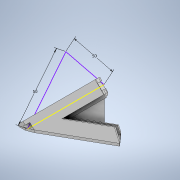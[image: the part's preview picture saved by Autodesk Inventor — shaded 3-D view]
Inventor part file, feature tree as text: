
AUTODESK INVENTOR PART (.ipt)
format: ipt  version: 2020 (Build 240168000, 168)  size: 267,776 bytes
history: native  units: mm
features: extrude x12, sketch x11, revolve x2, pattern_circular x1
ambient origin geometry x8: Origin, YZ Plane, XZ Plane, XY Plane, X Axis, Y Axis, Z Axis, Center Point
bodies: Solid1 (feature_tree)
feature tree (26):
  sketch  "Sketch1"  dims[d0=100.0mm d1=100.0mm]
  sketch  "Sketch2"  dims[d2=50.0mm d3=50.0mm]
  revolve  "Revolution1"  [1 undecoded]
  sketch  "Sketch3"  dims[d4=45.0deg d5=5.0mm d6=0.0mm]
  extrude  "Extrusion1"  Depth=50.0mm
  revolve  "Revolution2"  [1 undecoded]
  extrude  "Extrusion2"  Depth=5.0mm TaperAngle=0.0deg
  extrude  "Extrusion3"  Depth=5.0mm TaperAngle=90.0deg
  pattern_circular  "Circular Pattern1"  [2 undecoded]
  extrude  "Extrusion4"  Depth=5.0mm
  extrude  "Extrusion5"  Depth=2.0mm TaperAngle=0.0deg
  extrude  "Extrusion6"  Depth=27.0mm TaperAngle=0.0deg
  extrude  "Extrusion7"  Depth=2.0mm TaperAngle=0.0deg
  extrude  "Extrusion8"  [1 undecoded]
  extrude  "Extrusion9"  [1 undecoded]
  extrude  "Extrusion10"  [1 undecoded]
  extrude  "Extrusion11"  [1 undecoded]
  extrude  "Extrusion13"  [1 undecoded]
  sketch  "Sketch4"  dims[d7=45.0deg d8=5.0mm d9=0.0mm]
  sketch  "Sketch5"  dims[d10=5.0mm d11=0.0mm d12=20.0mm d13=90.0deg]
  sketch  "Sketch6"  dims[d15=7.0mm d16=0.0mm]
  sketch  "Sketch7"  dims[d17=44.0mm d18=0.0mm]
  sketch  "Sketch8"  dims[d19=3.0mm d20=0.0mm]
  sketch  "Sketch9"  dims[d21=2.0mm d22=0.0mm]
  sketch  "Sketch10"  dims[d23=5.0mm d24=0.0mm]
  sketch  "Sketch12"  dims[d25=4.0mm d26=11.0mm d27=0.0mm d28=5.0mm d29=11.0mm d30=0.0mm d31=27.0mm d32=0.0mm d35=2.0mm d36=0.0mm]
note: 9 required parameter values undecoded (feature->parameter linkage not recoverable at this tier; creation-order binding heuristic only, values carry confidence <= 0.55)